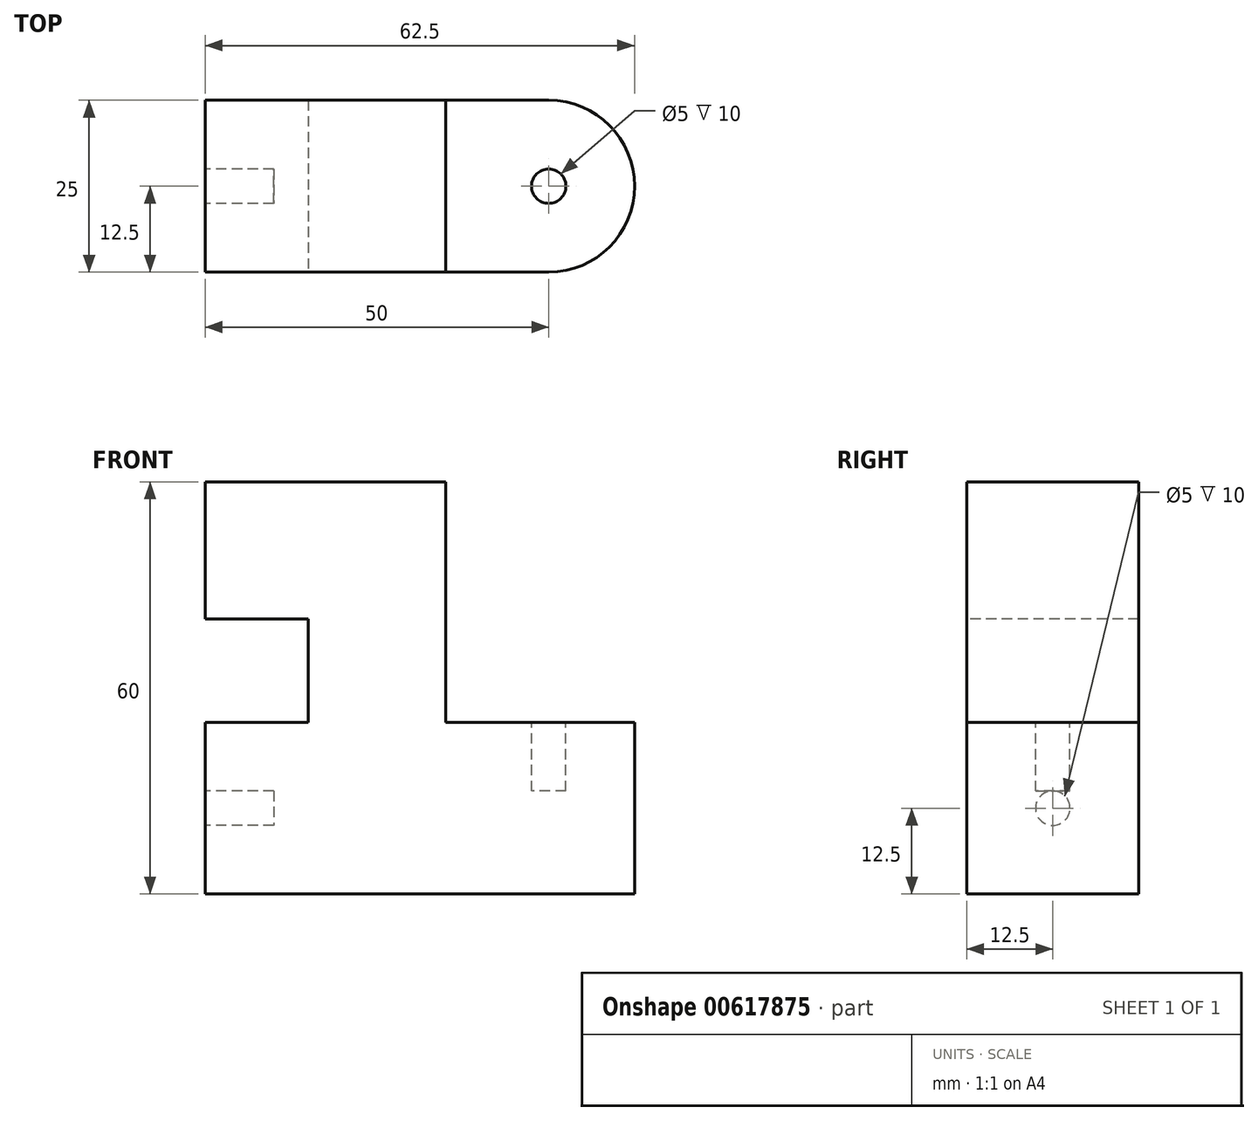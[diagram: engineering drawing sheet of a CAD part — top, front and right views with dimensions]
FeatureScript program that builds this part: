
annotation { "Feature Type Name" : "Feature", "Feature Type Description" : "" }
export const myFeature = defineFeature(function(context is Context, id is Id, definition is map)
    precondition{}
    {
        {
            var Q0;
            Q0=qCreatedBy(makeId("Top.planeOp"),FACE);
            var sketch = newSketch(context, id + "F0", { "sketchPlane" : qUnion([Q0])});
            skLineSegment(sketch, "E0.bottom", {"start": v(0, 0) * mm, "end": v(50, 0) * mm});
            skLineSegment(sketch, "E0.top", {"start": v(0, 25) * mm, "end": v(50, 25) * mm});
            skLineSegment(sketch, "E0.left", {"start": v(0, 0) * mm, "end": v(0, 25) * mm});
            skPoint(sketch, "E1.center.orphan", {"position": v(50, 12.5) * mm});
            skArc(sketch, "E2", {"start": v(50, 0) * mm, "mid": v(62.5, 12.5) * mm, "end": v(50, 25) * mm});
            skSolve(sketch);
        }
        {
            var Q0;
            Q0 = qSketchRegion(id + "F0", true);
            extrude(context, id + "F1", {"entities" : qUnion([Q0]), "depth" : 25 * mm, "offsetDistance" : 25 * mm});
        }
        {
            var Q0;
            Q0=makeQuery(id+"F1.opExtrude","CAP_FACE",FACE,{"disambiguationData":[OSD([sQuery(id+"F0.wireOp",EDGE,"E0.bottom"),sQuery(id+"F0.wireOp",EDGE,"E0.top"),sQuery(id+"F0.wireOp",EDGE,"E0.left"),sQuery(id+"F0.wireOp",EDGE,"E2")])],"isStart":false});
            var sketch = newSketch(context, id + "F2", { "sketchPlane" : qUnion([Q0])});
            skCircle(sketch, "E3", {"center": v(50, 12.5) * mm, "radius": 2.5 * mm});
            skSolve(sketch);
        }
        {
            var Q0;
            Q0 = qSketchRegion(id + "F2", true);
            extrude(context, id + "F3", {"entities" : qUnion([Q0]), "operationType" : NewBodyOperationType.REMOVE, "oppositeDirection" : true, "depth" : 10 * mm, "offsetDistance" : 25 * mm});
        }
        {
            var Q0;
            Q0=makeQuery(id+"F1.opExtrude","SWEPT_FACE",FACE,{"disambiguationData":[OSD([sQuery(id+"F0.wireOp",EDGE,"E0.left")])]});
            var sketch = newSketch(context, id + "F4", { "sketchPlane" : qUnion([Q0])});
            skCircle(sketch, "E4", {"center": v(-12.5, 12.5) * mm, "radius": 2.5 * mm});
            skPoint(sketch, "E4.centerSnap0", {"position": v(-25, 12.5) * mm});
            skPoint(sketch, "E4.centerSnap1", {"position": v(-12.5, 25) * mm});
            skSolve(sketch);
        }
        {
            var Q0;
            Q0 = qSketchRegion(id + "F4", true);
            extrude(context, id + "F5", {"entities" : qUnion([Q0]), "operationType" : NewBodyOperationType.REMOVE, "oppositeDirection" : true, "depth" : 10 * mm, "offsetDistance" : 25 * mm});
        }
        {
            var Q0;
            Q0=makeQuery(id+"F1.opExtrude","SWEPT_FACE",FACE,{"disambiguationData":[OSD([sQuery(id+"F0.wireOp",EDGE,"E0.bottom")])]});
            var sketch = newSketch(context, id + "F6", { "sketchPlane" : qUnion([Q0])});
            skLineSegment(sketch, "E5", {"start": v(15, 25) * mm, "end": v(15, 40) * mm});
            skLineSegment(sketch, "E6", {"start": v(15, 40) * mm, "end": v(0, 40) * mm});
            skLineSegment(sketch, "E7", {"start": v(0, 40) * mm, "end": v(0, 60) * mm});
            skLineSegment(sketch, "E8", {"start": v(0, 60) * mm, "end": v(35, 60) * mm});
            skLineSegment(sketch, "E9", {"start": v(35, 60) * mm, "end": v(35, 25) * mm});
            skLineSegment(sketch, "E10", {"start": v(35, 25) * mm, "end": v(15, 25) * mm});
            skSolve(sketch);
        }
        {
            var Q0;
            Q0 = qSketchRegion(id + "F6", true);
            extrude(context, id + "F7", {"entities" : qUnion([Q0]), "operationType" : NewBodyOperationType.ADD, "oppositeDirection" : true, "depth" : 25 * mm, "offsetDistance" : 25 * mm});
        }
    });
